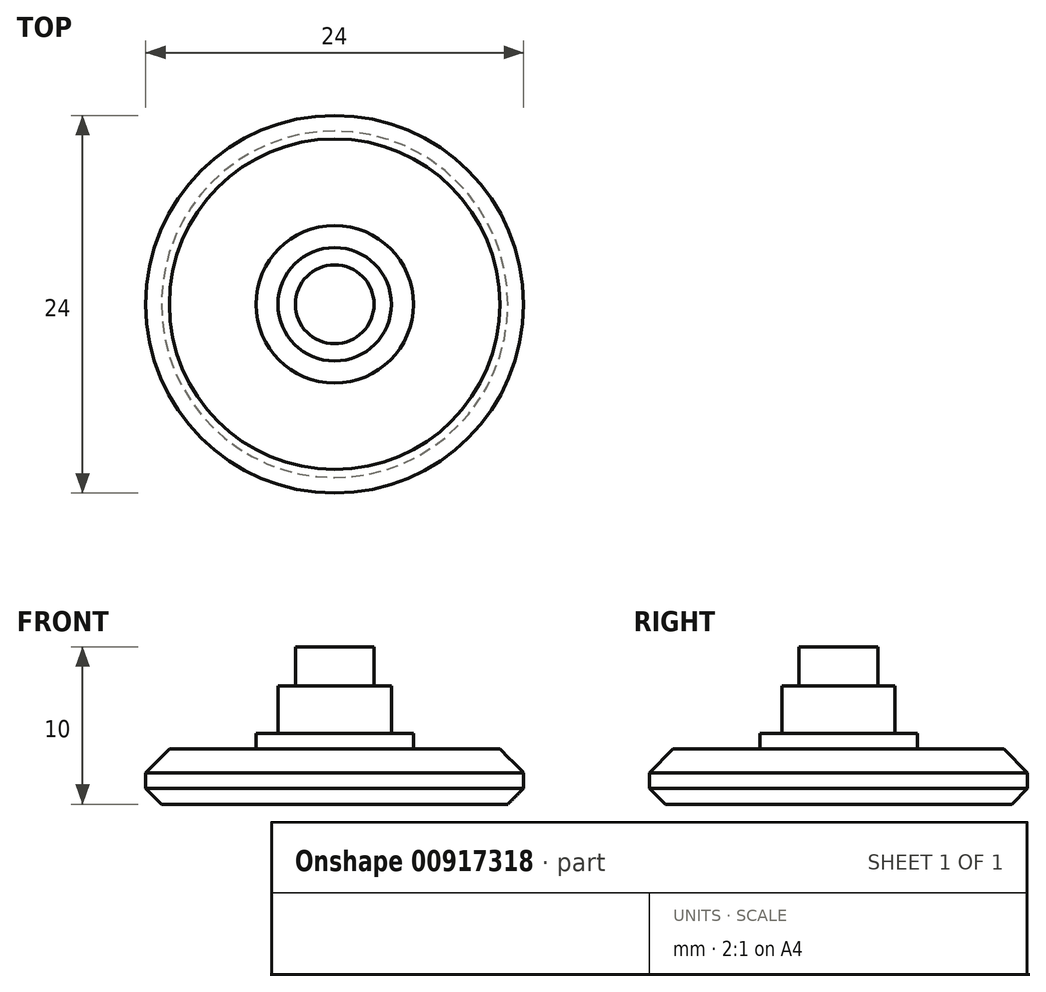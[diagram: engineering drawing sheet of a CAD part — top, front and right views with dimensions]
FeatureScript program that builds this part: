
annotation { "Feature Type Name" : "Feature", "Feature Type Description" : "" }
export const myFeature = defineFeature(function(context is Context, id is Id, definition is map)
    precondition{}
    {
        {
            var Q0;
            Q0=qCreatedBy(makeId("Top.planeOp"),FACE);
            var sketch = newSketch(context, id + "F0", { "sketchPlane" : qUnion([Q0])});
            skCircle(sketch, "E0", {"center": v(0, 0) * mm, "radius": 12 * mm});
            skCircle(sketch, "E1", {"center": v(0, 0) * mm, "radius": 11 * mm});
            skCircle(sketch, "E2", {"center": v(0, 0) * mm, "radius": 4.1 * mm});
            skCircle(sketch, "E3", {"center": v(0, 0) * mm, "radius": 3 * mm});
            skCircle(sketch, "E4", {"center": v(0, 0) * mm, "radius": 5 * mm});
            skSolve(sketch);
        }
        {
            var Q0;
            Q0=makeQuery(id+"F0.imprint","IMPRINT",FACE,{"disambiguationData":[TD([[makeQuery(id+"F0.imprint","IMPRINT",EDGE,{"derivedFrom":sQuery(id+"F0.wireOp",EDGE,"E0")}),1.0]])]});
            var Q1;
            Q1=makeQuery(id+"F0.imprint","IMPRINT",FACE,{"disambiguationData":[TD([[makeQuery(id+"F0.imprint","IMPRINT",EDGE,{"derivedFrom":sQuery(id+"F0.wireOp",EDGE,"E1")}),1.0]])]});
            var Q2;
            Q2=makeQuery(id+"F0.imprint","IMPRINT",FACE,{"disambiguationData":[TD([[makeQuery(id+"F0.imprint","IMPRINT",EDGE,{"derivedFrom":sQuery(id+"F0.wireOp",EDGE,"E3")}),1.0]])]});
            var Q3;
            Q3=makeQuery(id+"F0.imprint","IMPRINT",FACE,{"disambiguationData":[TD([[makeQuery(id+"F0.imprint","IMPRINT",EDGE,{"derivedFrom":sQuery(id+"F0.wireOp",EDGE,"E2")}),1.0]])]});
            var Q4;
            Q4=makeQuery(id+"F0.imprint","IMPRINT",FACE,{"disambiguationData":[TD([[makeQuery(id+"F0.imprint","IMPRINT",EDGE,{"derivedFrom":sQuery(id+"F0.wireOp",EDGE,"E2")}),-1.0]])]});
            extrude(context, id + "F1", {"entities" : qUnion([Q0, Q1, Q2, Q3, Q4]), "depth" : 2 * mm, "offsetDistance" : 25 * mm});
        }
        {
            var Q0;
            Q0=makeQuery(id+"F0.imprint","IMPRINT",FACE,{"disambiguationData":[TD([[makeQuery(id+"F0.imprint","IMPRINT",EDGE,{"derivedFrom":sQuery(id+"F0.wireOp",EDGE,"E1")}),1.0]])]});
            var Q1;
            Q1=makeQuery(id+"F0.imprint","IMPRINT",FACE,{"disambiguationData":[TD([[makeQuery(id+"F0.imprint","IMPRINT",EDGE,{"derivedFrom":sQuery(id+"F0.wireOp",EDGE,"E2")}),1.0]])]});
            var Q2;
            Q2=makeQuery(id+"F0.imprint","IMPRINT",FACE,{"disambiguationData":[TD([[makeQuery(id+"F0.imprint","IMPRINT",EDGE,{"derivedFrom":sQuery(id+"F0.wireOp",EDGE,"E3")}),1.0]])]});
            var Q3;
            Q3=makeQuery(id+"F0.imprint","IMPRINT",FACE,{"disambiguationData":[TD([[makeQuery(id+"F0.imprint","IMPRINT",EDGE,{"derivedFrom":sQuery(id+"F0.wireOp",EDGE,"E2")}),-1.0]])]});
            extrude(context, id + "F2", {"entities" : qUnion([Q0, Q1, Q2, Q3]), "operationType" : NewBodyOperationType.ADD, "depth" : 3.5 * mm, "offsetDistance" : 25 * mm});
        }
        {
            var Q0;
            Q0=makeQuery(id+"F2.boolean.opBoolean","INTERSECT",EDGE,{"derivedFrom":[makeQuery(id+"F1.opExtrude","CAP_FACE",FACE,{"disambiguationData":[OSD([sQuery(id+"F0.wireOp",EDGE,"E0")])],"isStart":false}),makeQuery(id+"F2.opExtrude","SWEPT_FACE",FACE,{"disambiguationData":[OSD([sQuery(id+"F0.wireOp",EDGE,"E1")])]})]});
            chamfer(context, id + "F3", {"entities" : qUnion([Q0]), "width" : 1 * mm, "tangentPropagation" : true});
        }
        {
            var Q0;
            Q0=makeQuery(id+"F0.imprint","IMPRINT",FACE,{"disambiguationData":[TD([[makeQuery(id+"F0.imprint","IMPRINT",EDGE,{"derivedFrom":sQuery(id+"F0.wireOp",EDGE,"E3")}),1.0]])]});
            var Q1;
            Q1=makeQuery(id+"F0.imprint","IMPRINT",FACE,{"disambiguationData":[TD([[makeQuery(id+"F0.imprint","IMPRINT",EDGE,{"derivedFrom":sQuery(id+"F0.wireOp",EDGE,"E2")}),1.0]])]});
            var Q2;
            Q2=makeQuery(id+"F0.imprint","IMPRINT",FACE,{"disambiguationData":[TD([[makeQuery(id+"F0.imprint","IMPRINT",EDGE,{"derivedFrom":sQuery(id+"F0.wireOp",EDGE,"E2")}),-1.0]])]});
            extrude(context, id + "F4", {"entities" : qUnion([Q0, Q1, Q2]), "operationType" : NewBodyOperationType.ADD, "depth" : 4.5 * mm, "offsetDistance" : 25 * mm});
        }
        {
            var Q0;
            Q0=makeQuery(id+"F0.imprint","IMPRINT",FACE,{"disambiguationData":[TD([[makeQuery(id+"F0.imprint","IMPRINT",EDGE,{"derivedFrom":sQuery(id+"F0.wireOp",EDGE,"E2")}),1.0]])]});
            extrude(context, id + "F5", {"entities" : qUnion([Q0]), "operationType" : NewBodyOperationType.ADD, "depth" : 7.5 * mm, "offsetDistance" : 25 * mm});
        }
        {
            var Q0;
            Q0=makeQuery(id+"F0.imprint","IMPRINT",FACE,{"disambiguationData":[TD([[makeQuery(id+"F0.imprint","IMPRINT",EDGE,{"derivedFrom":sQuery(id+"F0.wireOp",EDGE,"E3")}),1.0]])]});
            extrude(context, id + "F6", {"entities" : qUnion([Q0]), "operationType" : NewBodyOperationType.ADD, "depth" : 10 * mm, "offsetDistance" : 25 * mm});
        }
        {
            var Q0;
            Q0=makeQuery(id+"F1.opExtrude","CAP_EDGE",EDGE,{"disambiguationData":[OSD([sQuery(id+"F0.wireOp",EDGE,"E0")])],"isStart":true});
            chamfer(context, id + "F7", {"entities" : qUnion([Q0]), "width" : 1 * mm, "tangentPropagation" : true});
        }
        {
            var Q0;
            Q0=makeQuery(id+"F2.opExtrude","CAP_EDGE",EDGE,{"disambiguationData":[OSD([sQuery(id+"F0.wireOp",EDGE,"E1")])],"isStart":false});
            chamfer(context, id + "F8", {"entities" : qUnion([Q0]), "width" : 0.5 * mm, "tangentPropagation" : true});
        }
        {
            var Q0;
            Q0=makeQuery(id+"F6.opExtrude","CAP_FACE",FACE,{"disambiguationData":[OSD([sQuery(id+"F0.wireOp",EDGE,"E3")])],"isStart":false});
            var sketch = newSketch(context, id + "F9", { "sketchPlane" : qUnion([Q0])});
            skCircle(sketch, "E5.0", {"center": v(0, 0) * mm, "radius": 3 * mm});
            skCircle(sketch, "E6.0", {"center": v(0, 0) * mm, "radius": 2.5 * mm});
            skSolve(sketch);
        }
        {
            var Q0;
            Q0=qSketchRegion(id+"F9",true);
            var Q1;
            Q1=makeQuery(id+"F5.opExtrude","CAP_FACE",FACE,{"disambiguationData":[OSD([sQuery(id+"F0.wireOp",EDGE,"E2"),sQuery(id+"F0.wireOp",EDGE,"E3")])],"isStart":false});
            extrude(context, id + "F10", {"entities" : qUnion([Q0]), "operationType" : NewBodyOperationType.REMOVE, "endBound" : BoundingType.UP_TO_SURFACE, "oppositeDirection" : true, "depth" : 25 * mm, "endBoundEntityFace" : qUnion([Q1]), "offsetDistance" : 25 * mm});
        }
        {
            var Q0;
            Q0=makeQuery(id+"F10.boolean.opBoolean","MERGE",FACE,{"derivedFrom":[makeQuery(id+"F5.opExtrude","CAP_FACE",FACE,{"disambiguationData":[OSD([sQuery(id+"F0.wireOp",EDGE,"E2"),sQuery(id+"F0.wireOp",EDGE,"E3")])],"isStart":false})],"fromTools":[makeQuery(id+"F10.opExtrude","CAP_FACE",FACE,{"disambiguationData":[OSD([sQuery(id+"F9.wireOp",EDGE,"E5.0"),sQuery(id+"F9.wireOp",EDGE,"E6.0")])],"isStart":false})]});
            var sketch = newSketch(context, id + "F11", { "sketchPlane" : qUnion([Q0])});
            skCircle(sketch, "E7.0", {"center": v(0, 0) * mm, "radius": 4.1 * mm});
            skCircle(sketch, "E8.0", {"center": v(0, 0) * mm, "radius": 3.6 * mm});
            skSolve(sketch);
        }
        {
            var Q0;
            Q0=qSketchRegion(id+"F11",true);
            var Q1;
            {var subQ0=sQuery(id+"F0.wireOp",EDGE,"E4");Q1=makeQuery(id+"F5.boolean.opBoolean","SPLIT",FACE,{"disambiguationData":[TD([makeQuery(id+"F4.opExtrude","SWEPT_FACE",FACE,{"disambiguationData":[OSD([subQ0])]})])],"derivedFrom":makeQuery(id+"F4.opExtrude","CAP_FACE",FACE,{"disambiguationData":[OSD([subQ0])],"isStart":false})});}
            extrude(context, id + "F12", {"entities" : qUnion([Q0]), "operationType" : NewBodyOperationType.REMOVE, "endBound" : BoundingType.UP_TO_SURFACE, "oppositeDirection" : true, "depth" : 25 * mm, "endBoundEntityFace" : qUnion([Q1]), "offsetDistance" : 25 * mm});
        }
    });
